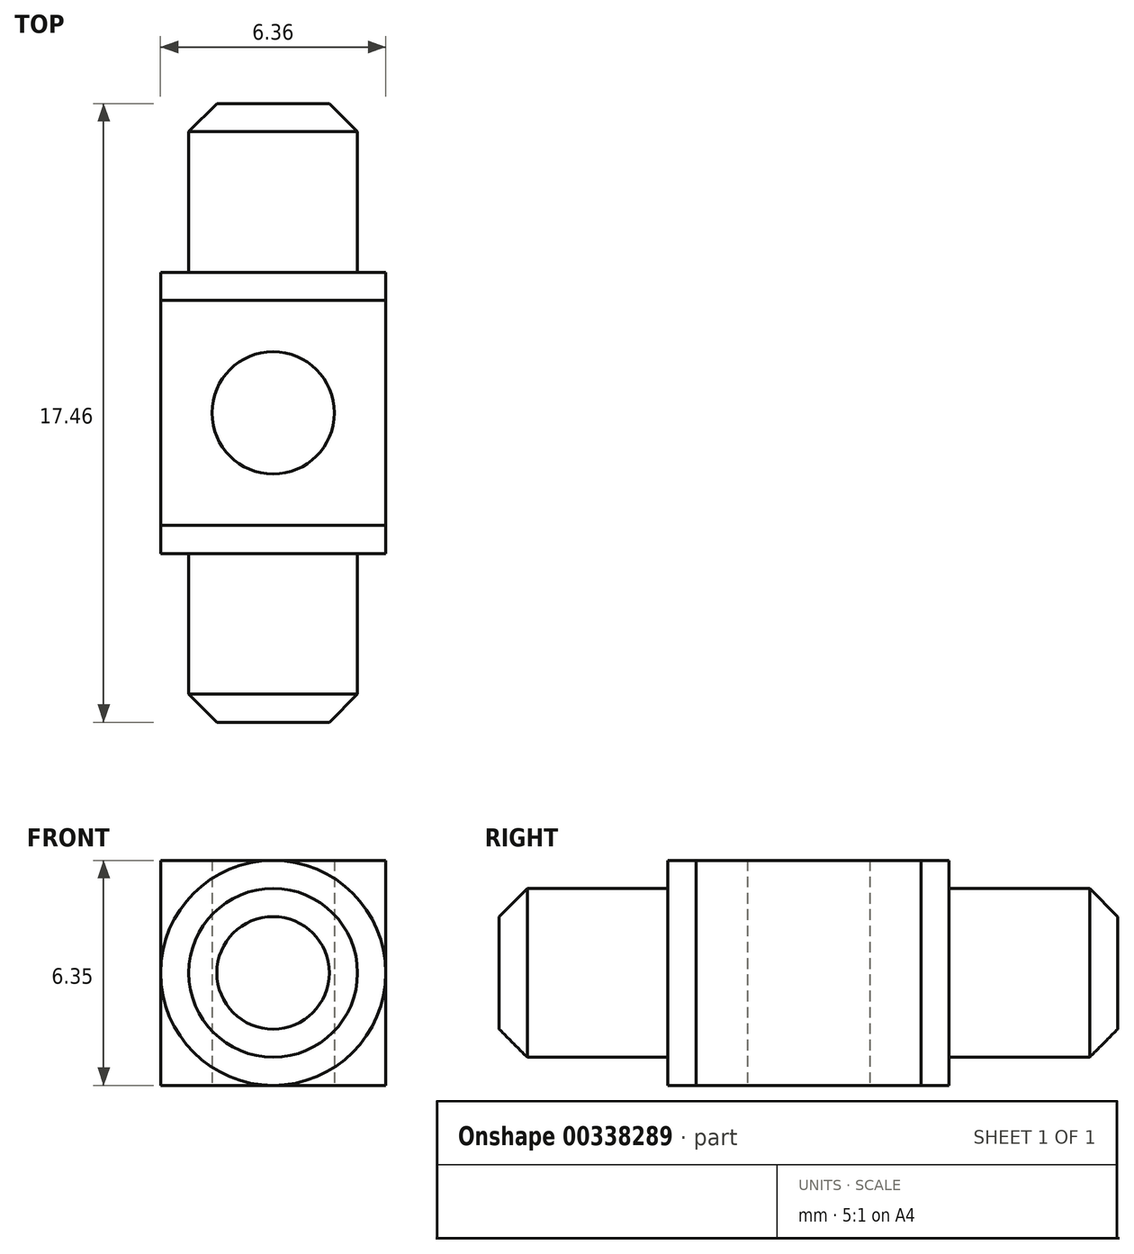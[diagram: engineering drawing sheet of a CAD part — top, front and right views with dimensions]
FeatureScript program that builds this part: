
annotation { "Feature Type Name" : "Feature", "Feature Type Description" : "" }
export const myFeature = defineFeature(function(context is Context, id is Id, definition is map)
    precondition{}
    {
        {
            var Q0;
            Q0=qCreatedBy(makeId("Top.planeOp"),FACE);
            var sketch = newSketch(context, id + "F0", { "sketchPlane" : qUnion([Q0])});
            skLineSegment(sketch, "E0.bottom", {"start": v(3.18, 3.18) * mm, "end": v(-3.18, 3.18) * mm});
            skLineSegment(sketch, "E0.top", {"start": v(3.18, -3.18) * mm, "end": v(-3.18, -3.18) * mm});
            skLineSegment(sketch, "E0.left", {"start": v(3.17, 3.18) * mm, "end": v(3.18, -3.18) * mm});
            skLineSegment(sketch, "E0.right", {"start": v(-3.18, 3.18) * mm, "end": v(-3.17, -3.18) * mm});
            skPoint(sketch, "E0.middle", {"position": v(0, 0) * mm});
            skSolve(sketch);
        }
        {
            var Q0;
            Q0=qSketchRegion(id+"F0",true);
            extrude(context, id + "F1", {"entities" : qUnion([Q0]), "depth" : 6.35 * mm});
        }
        {
            var Q0;
            Q0=qCreatedBy(makeId("Front.planeOp"),FACE);
            var sketch = newSketch(context, id + "F2", { "sketchPlane" : qUnion([Q0])});
            skCircle(sketch, "E1", {"center": v(0, 3.18) * mm, "radius": 3.18 * mm});
            skLineSegment(sketch, "E2", {"start": v(0, 0) * mm, "end": v(0, 6.35) * mm, "construction": true});
            skSolve(sketch);
        }
        {
            var Q0;
            Q0=qSketchRegion(id+"F2",true);
            extrude(context, id + "F3", {"entities" : qUnion([Q0]), "operationType" : NewBodyOperationType.ADD, "depth" : 7.94 * mm, "symmetric" : true});
        }
        {
            var Q0;
            Q0=qCreatedBy(makeId("Front.planeOp"),FACE);
            var sketch = newSketch(context, id + "F4", { "sketchPlane" : qUnion([Q0])});
            skCircle(sketch, "E3", {"center": v(0, 3.18) * mm, "radius": 2.38 * mm});
            skSolve(sketch);
        }
        {
            var Q0;
            Q0=qSketchRegion(id+"F4",true);
            extrude(context, id + "F5", {"entities" : qUnion([Q0]), "operationType" : NewBodyOperationType.ADD, "depth" : 17.46 * mm, "symmetric" : true});
        }
        {
            var Q0;
            Q0=makeQuery(id+"F1.opExtrude","CAP_FACE",FACE,{"disambiguationData":[OSD([sQuery(id+"F0.wireOp",EDGE,"E0.bottom"),sQuery(id+"F0.wireOp",EDGE,"E0.top"),sQuery(id+"F0.wireOp",EDGE,"E0.left"),sQuery(id+"F0.wireOp",EDGE,"E0.right")])],"isStart":true});
            var sketch = newSketch(context, id + "F6", { "sketchPlane" : qUnion([Q0])});
            skCircle(sketch, "E4", {"center": v(0, 0) * mm, "radius": 1.73 * mm});
            skSolve(sketch);
        }
        {
            var Q0;
            Q0=qSketchRegion(id+"F6",true);
            var Q1;
            Q1=makeQuery(id+"F1.opExtrude","CAP_FACE",FACE,{"disambiguationData":[OSD([sQuery(id+"F0.wireOp",EDGE,"E0.bottom"),sQuery(id+"F0.wireOp",EDGE,"E0.top"),sQuery(id+"F0.wireOp",EDGE,"E0.left"),sQuery(id+"F0.wireOp",EDGE,"E0.right")])],"isStart":false});
            extrude(context, id + "F7", {"entities" : qUnion([Q0]), "operationType" : NewBodyOperationType.REMOVE, "endBound" : BoundingType.UP_TO_SURFACE, "oppositeDirection" : true, "endBoundEntityFace" : qUnion([Q1]), "depth" : 25.4 * mm});
        }
        {
            var Q0;
            Q0=makeQuery(id+"F5.opExtrude","CAP_EDGE",EDGE,{"disambiguationData":[OSD([sQuery(id+"F4.wireOp",EDGE,"E3")])],"isStart":false});
            var Q1;
            Q1=makeQuery(id+"F5.opExtrude","CAP_EDGE",EDGE,{"disambiguationData":[OSD([sQuery(id+"F4.wireOp",EDGE,"E3")])],"isStart":true});
            chamfer(context, id + "F8", {"entities" : qUnion([Q0, Q1]), "width" : 0.8 * mm, "tangentPropagation" : true});
        }
    });
